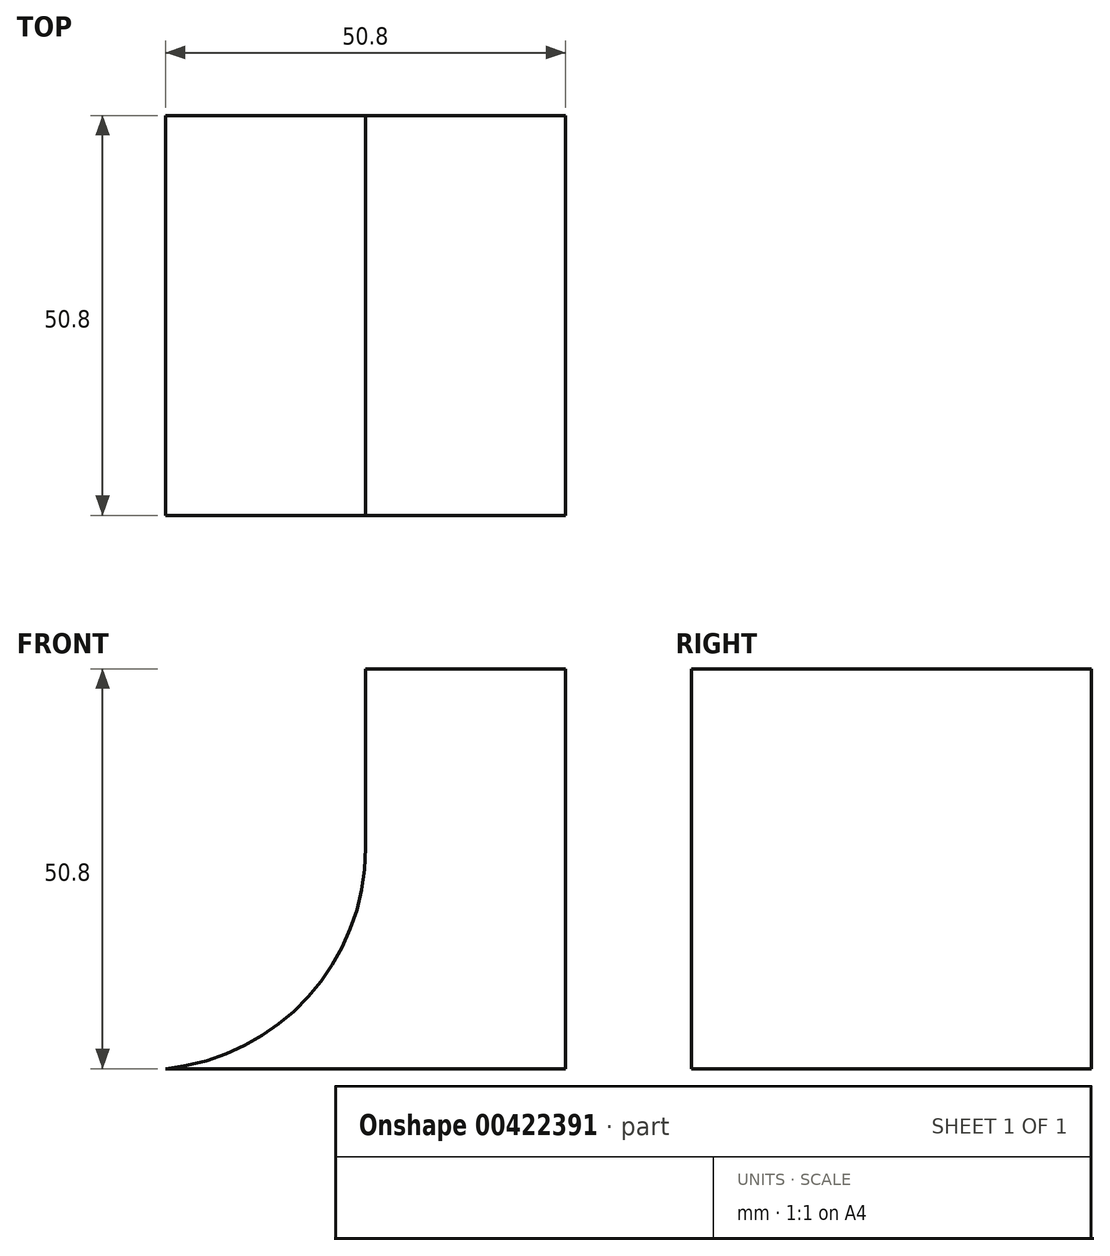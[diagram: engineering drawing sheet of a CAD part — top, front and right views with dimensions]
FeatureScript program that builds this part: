
annotation { "Feature Type Name" : "Feature", "Feature Type Description" : "" }
export const myFeature = defineFeature(function(context is Context, id is Id, definition is map)
    precondition{}
    {
        {
            var Q0;
            Q0=qCreatedBy(makeId("Front.planeOp"),FACE);
            var sketch = newSketch(context, id + "F0", { "sketchPlane" : qUnion([Q0])});
            skLineSegment(sketch, "E0", {"start": v(0, 0) * mm, "end": v(0, 50.8) * mm});
            skLineSegment(sketch, "E1", {"start": v(0, 50.8) * mm, "end": v(-25.4, 50.8) * mm});
            skLineSegment(sketch, "E2", {"start": v(-25.4, 50.8) * mm, "end": v(-25.4, 28.02) * mm});
            skLineSegment(sketch, "E3", {"start": v(-50.8, 0) * mm, "end": v(0, 0) * mm});
            skArc(sketch, "E4", {"start": v(-50.8, 0) * mm, "mid": v(-32.7, 9.1) * mm, "end": v(-25.4, 28.02) * mm});
            skSolve(sketch);
        }
        {
            var Q0;
            Q0 = qSketchRegion(id + "F0", true);
            extrude(context, id + "F1", {"entities" : qUnion([Q0]), "depth" : 50.8 * mm});
        }
    });
